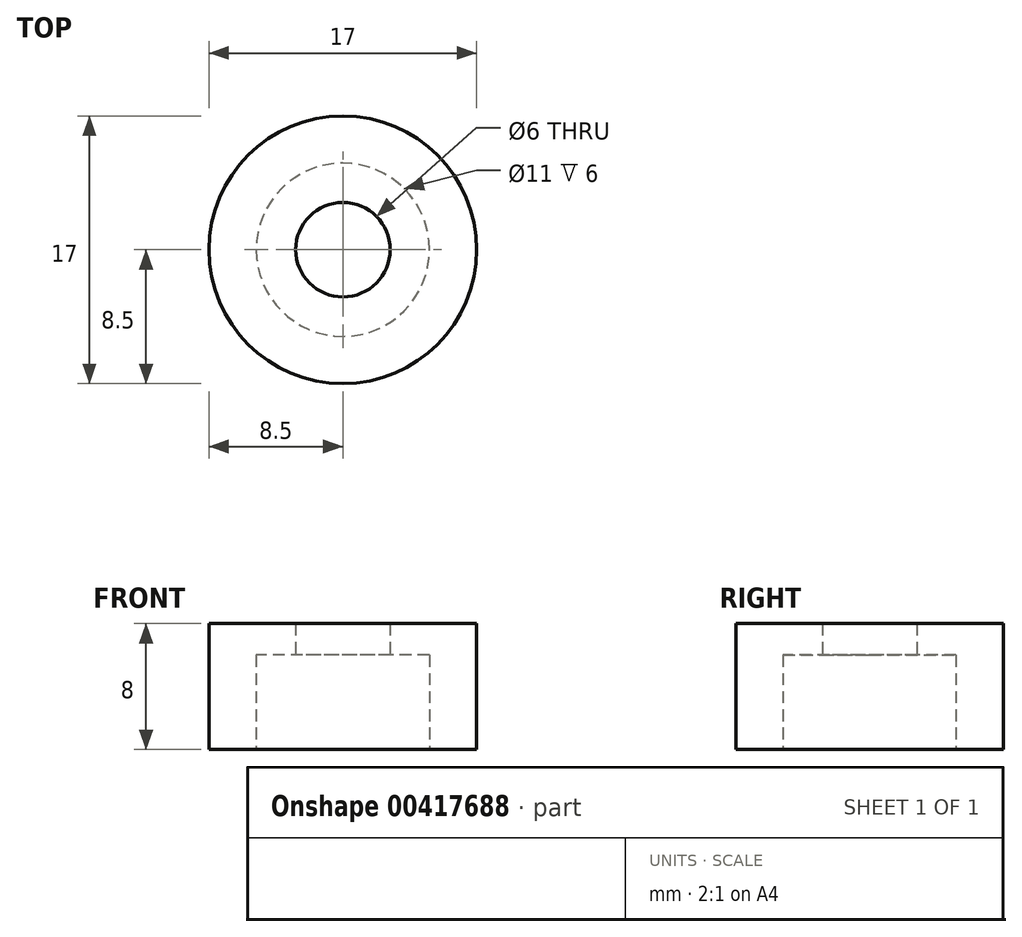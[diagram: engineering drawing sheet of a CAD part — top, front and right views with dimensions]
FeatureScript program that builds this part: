
annotation { "Feature Type Name" : "Feature", "Feature Type Description" : "" }
export const myFeature = defineFeature(function(context is Context, id is Id, definition is map)
    precondition{}
    {
        {
            var Q0;
            Q0=qCreatedBy(makeId("Top.planeOp"),FACE);
            var sketch = newSketch(context, id + "F0", { "sketchPlane" : qUnion([Q0])});
            skCircle(sketch, "E0", {"center": v(0, 0) * mm, "radius": 8.5 * mm});
            skCircle(sketch, "E1", {"center": v(0, 0) * mm, "radius": 5.5 * mm});
            skCircle(sketch, "E2", {"center": v(0, 0) * mm, "radius": 3 * mm});
            skSolve(sketch);
        }
        {
            var Q0;
            Q0=makeQuery(id+"F0.imprint","IMPRINT",FACE,{"disambiguationData":[TD([[makeQuery(id+"F0.imprint","IMPRINT",EDGE,{"derivedFrom":sQuery(id+"F0.wireOp",EDGE,"E0")}),1.0]])]});
            extrude(context, id + "F1", {"entities" : qUnion([Q0]), "depth" : 8 * mm});
        }
        {
            var Q0;
            Q0=makeQuery(id+"F0.imprint","IMPRINT",FACE,{"disambiguationData":[TD([[makeQuery(id+"F0.imprint","IMPRINT",EDGE,{"derivedFrom":sQuery(id+"F0.wireOp",EDGE,"E1")}),1.0]])]});
            extrude(context, id + "F2", {"entities" : qUnion([Q0]), "operationType" : NewBodyOperationType.ADD, "depth" : 8 * mm});
        }
        {
            var Q0;
            Q0=makeQuery(id+"F0.imprint","IMPRINT",FACE,{"disambiguationData":[TD([[makeQuery(id+"F0.imprint","IMPRINT",EDGE,{"derivedFrom":sQuery(id+"F0.wireOp",EDGE,"E1")}),1.0]])]});
            extrude(context, id + "F3", {"entities" : qUnion([Q0]), "operationType" : NewBodyOperationType.REMOVE, "depth" : 6 * mm});
        }
    });
